# Revit family: QF_BOURGEAT_OPTIMO_Gamme_standard_Démontables
name_source: partatom
category: Equipement spécialisé
revit_build: Autodesk Revit 2015 (Build: 20140606_1530(x64)
units: mm (PartAtom-declared; Revit-internal decimal feet)

## types (8) — shared parameters
Charge max = 200.00 kg
Charge maximale = 20 kg par glissière; 200kg par chariot
Fabricant = BOURGEAT
Hauteur barre de renfort GN 1 = 358 mm  [stored 1.17454 ft]
Hauteur barre de renfort GN 2 = 492 mm  [stored 1.61417 ft]
Hauteur echelle = 1487 mm  [stored 4.87861 ft]
Hauteur hors tout = 1650 mm  [stored 5.41339 ft]
Poids net à vide = 0.00 kg
Spécification du Fabricant = Chariot à glissières démontables
URL catalogue = http://www.bourgeat.fr

## per-type parameters (varying)
| type | Barre de renfort milieu GN2/1 | Barre renfort | Entrée | Longueur hors tout | Modèle | Niveaux | Profondeur echelle | Profondeur hors tout |
| GN1/1-15 niveaux - Espacement 89 mm | Non | 335 mm  [stored 1.09908 ft] | 325 mm  [stored 1.06627 ft] | 460 mm  [stored 1.50919 ft] | 775615 | 15 | 555 mm  [stored 1.82087 ft] | 630 mm  [stored 2.06693 ft] |
| GN1/1-20 niveaux - Espacement 67 mm | Non | 335 mm  [stored 1.09908 ft] | 325 mm  [stored 1.06627 ft] | 460 mm  [stored 1.50919 ft] | 775620 | 20 | 555 mm  [stored 1.82087 ft] | 630 mm  [stored 2.06693 ft] |
| GN2/1-15 niveaux - Espacement 89 mm | Oui | 535 mm | 530 mm  [stored 1.73885 ft] | 660 mm | 774615 | 15 | 675 mm  [stored 2.21457 ft] | 750 mm  [stored 2.46063 ft] |
| GN2/1-20 niveaux - Espacement 67 mm | Oui | 535 mm | 530 mm  [stored 1.73885 ft] | 660 mm | 774620 | 20 | 675 mm  [stored 2.21457 ft] | 750 mm  [stored 2.46063 ft] |
| "Pâtissier" 600x400-15 niveaux - Espacement 89 mm | Non | 405 mm  [stored 1.32874 ft] | 400 mm  [stored 1.31234 ft] | 530 mm  [stored 1.73885 ft] | 772815 | 15 | 625 mm  [stored 2.05052 ft] | 700 mm  [stored 2.29659 ft] |
| "Pâtissier" 600x400-20 niveaux - Espacement 67 mm | Non | 405 mm  [stored 1.32874 ft] | 400 mm  [stored 1.31234 ft] | 530 mm  [stored 1.73885 ft] | 772820 | 20 | 625 mm  [stored 2.05052 ft] | 700 mm  [stored 2.29659 ft] |
| "Pâtissier" 400x600-15 niveaux - Espacement 89 mm | Non | 605 mm  [stored 1.98491 ft] | 600 mm | 730 mm  [stored 2.39501 ft] | 773815 | 15 | 425 mm  [stored 1.39436 ft] | 500 mm  [stored 1.64042 ft] |
| "Pâtissier" 400x600-20 niveaux - Espacement 67 mm | Non | 605 mm  [stored 1.98491 ft] | 600 mm | 730 mm  [stored 2.39501 ft] | 773820 | 20 | 425 mm  [stored 1.39436 ft] | 500 mm  [stored 1.64042 ft] |

note: [stored X ft] marks values corroborated as IEEE doubles in the binary element streams (Revit-internal decimal feet)
